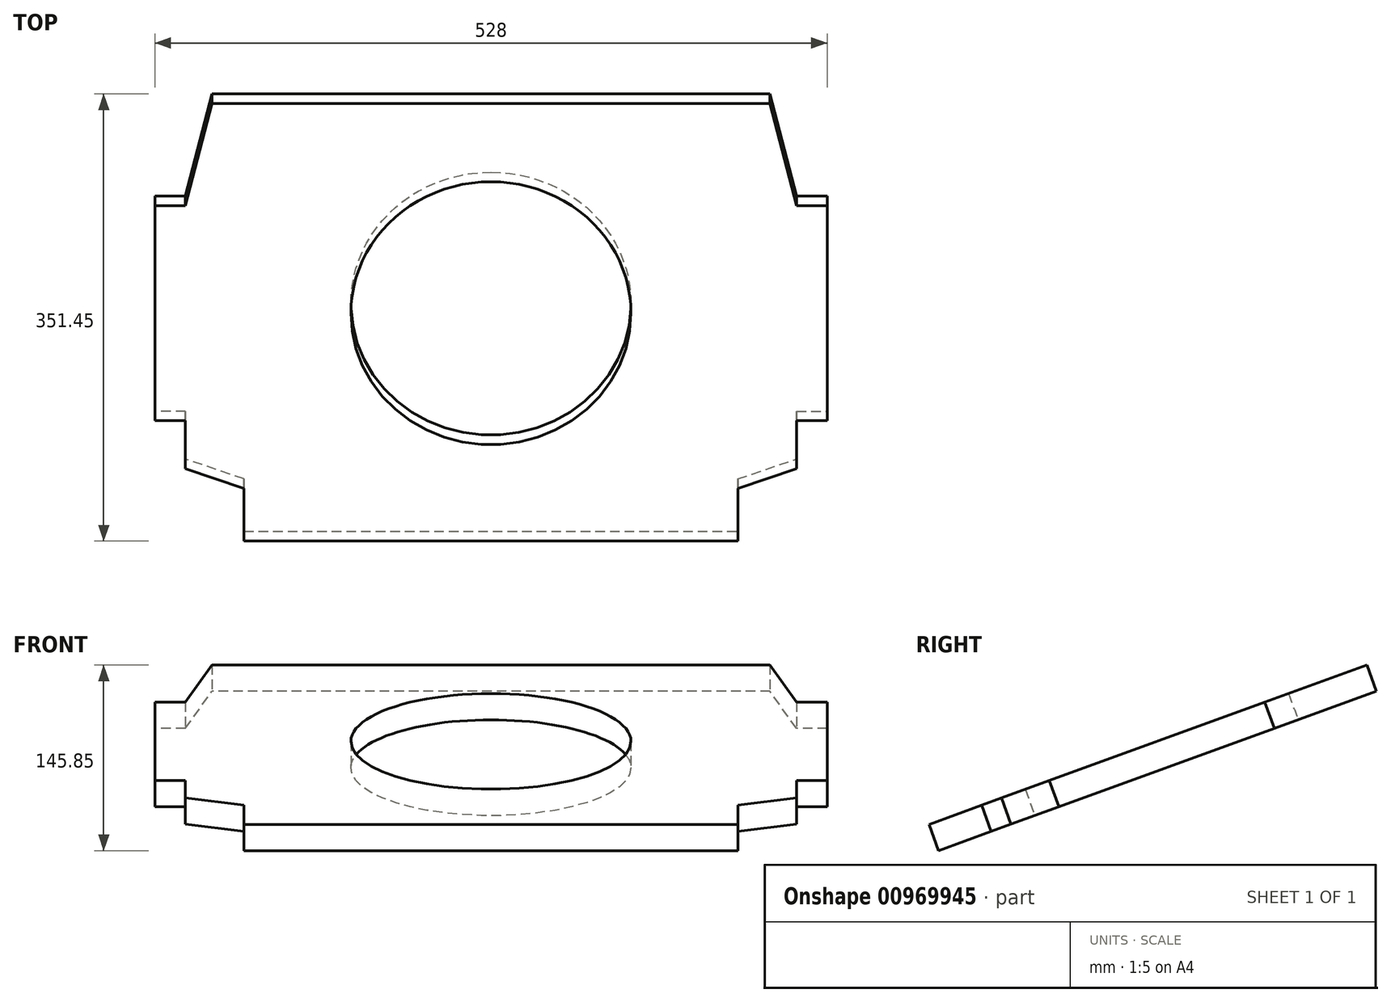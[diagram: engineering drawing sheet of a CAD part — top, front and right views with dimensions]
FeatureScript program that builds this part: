
annotation { "Feature Type Name" : "Feature", "Feature Type Description" : "" }
export const myFeature = defineFeature(function(context is Context, id is Id, definition is map)
    precondition{}
    {
        {
            var Q0;
            Q0=qCreatedBy(makeId("Top.planeOp"),FACE);
            var sketch = newSketch(context, id + "F0", { "sketchPlane" : qUnion([Q0])});
            skLineSegment(sketch, "E0", {"start": v(0, 0) * mm, "end": v(70.27, 0) * mm});
            skSolve(sketch);
        }
        {
            var Q0;
            Q0=qCreatedBy(makeId("Top.planeOp"),FACE);
            var Q1;
            Q1=sQuery(id+"F0.wireOp",EDGE,"E0");
            cPlane(context, id + "F1", {"entities" : qUnion([Q0, Q1]), "cplaneType" : CPlaneType.LINE_ANGLE, "offset" : 25 * mm, "angle" : 20 * degree, "width" : 150 * mm, "height" : 150 * mm});
        }
        {
            var Q0;
            Q0=qCreatedBy(id+"F1.planeOp",FACE);
            var sketch = newSketch(context, id + "F2", { "sketchPlane" : qUnion([Q0])});
            skLineSegment(sketch, "E1", {"start": v(-194, 139) * mm, "end": v(-194, 183) * mm});
            skLineSegment(sketch, "E2", {"start": v(194, 139) * mm, "end": v(194, 183) * mm});
            skCircle(sketch, "E3", {"center": v(0, -7.57) * mm, "radius": 110 * mm});
            skLineSegment(sketch, "E4", {"start": v(240, 82.43) * mm, "end": v(240, 122.43) * mm});
            skLineSegment(sketch, "E5", {"start": v(264, -97.57) * mm, "end": v(264, 82.43) * mm});
            skLineSegment(sketch, "E6", {"start": v(240, 82.43) * mm, "end": v(264, 82.43) * mm});
            skLineSegment(sketch, "E7", {"start": v(194, 139) * mm, "end": v(240, 122.43) * mm});
            skLineSegment(sketch, "E8", {"start": v(-240, 82.43) * mm, "end": v(-240, 122.43) * mm});
            skLineSegment(sketch, "E9", {"start": v(-264, -97.57) * mm, "end": v(-264, 82.43) * mm});
            skLineSegment(sketch, "E10", {"start": v(-240, 82.43) * mm, "end": v(-264, 82.43) * mm});
            skLineSegment(sketch, "E11", {"start": v(-194, 139) * mm, "end": v(-240, 122.43) * mm});
            skLineSegment(sketch, "E12", {"start": v(-240, -97.57) * mm, "end": v(-264, -97.57) * mm});
            skLineSegment(sketch, "E13", {"start": v(264, -97.57) * mm, "end": v(240, -97.57) * mm});
            skLineSegment(sketch, "E14", {"start": v(-160, -183) * mm, "end": v(160, -183) * mm});
            skLineSegment(sketch, "E15", {"start": v(-194, 183) * mm, "end": v(194, 183) * mm});
            skLineSegment(sketch, "E16", {"start": v(-160, -183) * mm, "end": v(-219.13, -183) * mm});
            skLineSegment(sketch, "E17", {"start": v(160, -183) * mm, "end": v(219.13, -183) * mm});
            skLineSegment(sketch, "E18", {"start": v(-240, -97.57) * mm, "end": v(-219.13, -183) * mm});
            skLineSegment(sketch, "E19", {"start": v(240, -97.57) * mm, "end": v(219.13, -183) * mm});
            skSolve(sketch);
        }
        {
            var Q0;
            Q0=makeQuery(id+"F2.imprint","IMPRINT",FACE,{"disambiguationData":[TD([[makeQuery(id+"F2.imprint","IMPRINT",EDGE,{"derivedFrom":sQuery(id+"F2.wireOp",EDGE,"E1")}),-1.0]])]});
            extrude(context, id + "F3", {"entities" : qUnion([Q0]), "oppositeDirection" : true, "depth" : 22 * mm, "offsetDistance" : 25 * mm});
        }
    });
